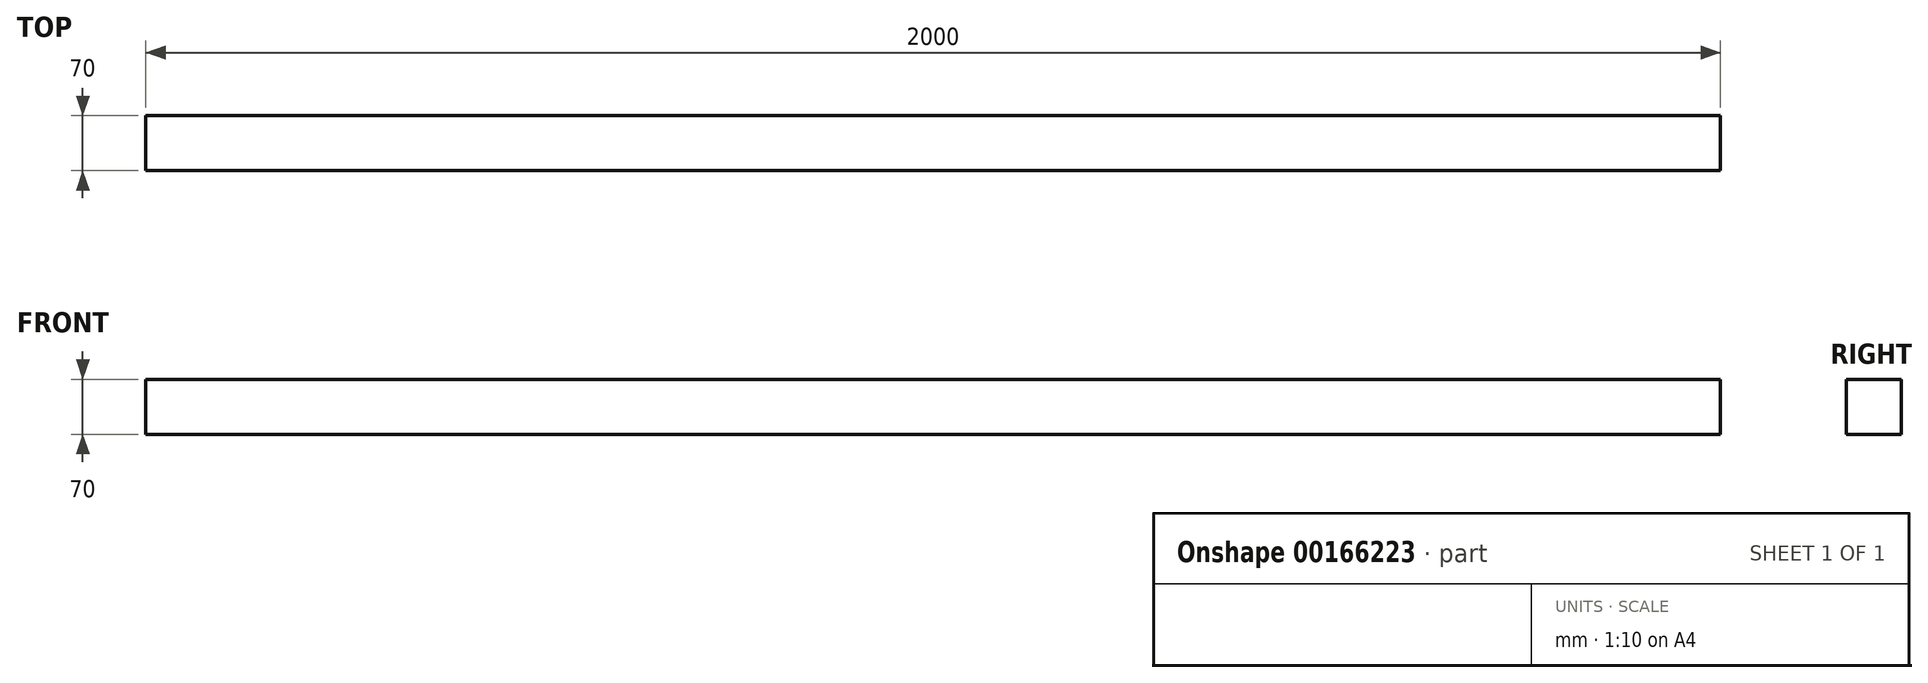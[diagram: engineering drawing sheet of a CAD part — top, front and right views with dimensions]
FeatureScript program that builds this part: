
annotation { "Feature Type Name" : "Feature", "Feature Type Description" : "" }
export const myFeature = defineFeature(function(context is Context, id is Id, definition is map)
    precondition{}
    {
        {
            var Q0;
            Q0=qCreatedBy(makeId("Front.planeOp"),FACE);
            var sketch = newSketch(context, id + "F0", { "sketchPlane" : qUnion([Q0])});
            skLineSegment(sketch, "E0.bottom", {"start": v(-1000, -35) * mm, "end": v(1000, -35) * mm});
            skLineSegment(sketch, "E0.top", {"start": v(-1000, 35) * mm, "end": v(1000, 35) * mm});
            skLineSegment(sketch, "E0.left", {"start": v(-1000, -35) * mm, "end": v(-1000, 35) * mm});
            skLineSegment(sketch, "E0.right", {"start": v(1000, -35) * mm, "end": v(1000, 35) * mm});
            skPoint(sketch, "E0.middle", {"position": v(0, 0) * mm});
            skSolve(sketch);
        }
        {
            var Q0;
            Q0=makeQuery(id+"F0.imprint","IMPRINT",FACE,{"disambiguationData":[TD([[makeQuery(id+"F0.imprint","IMPRINT",EDGE,{"derivedFrom":sQuery(id+"F0.wireOp",EDGE,"E0.bottom")}),1.0]])]});
            extrude(context, id + "F1", {"entities" : qUnion([Q0]), "depth" : 70 * mm, "symmetric" : true});
        }
    });
